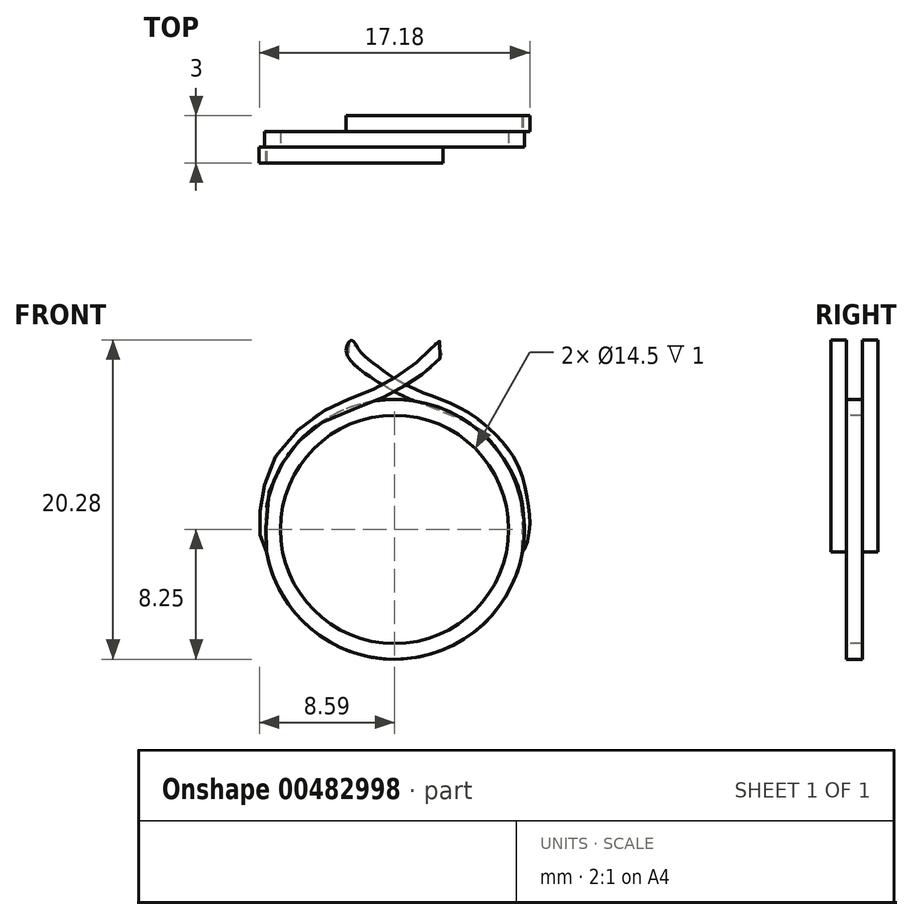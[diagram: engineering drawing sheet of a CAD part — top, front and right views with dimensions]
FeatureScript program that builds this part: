
annotation { "Feature Type Name" : "Feature", "Feature Type Description" : "" }
export const myFeature = defineFeature(function(context is Context, id is Id, definition is map)
    precondition{}
    {
        {
            var Q0;
            Q0=qCreatedBy(makeId("Front.planeOp"),FACE);
            var sketch = newSketch(context, id + "F0", { "sketchPlane" : qUnion([Q0])});
            skCircle(sketch, "E0", {"center": v(0, 0) * mm, "radius": 7.25 * mm});
            skCircle(sketch, "E1", {"center": v(0, 0) * mm, "radius": 8.25 * mm});
            skSolve(sketch);
        }
        {
            var Q0;
            Q0 = qSketchRegion(id + "F0", true);
            extrude(context, id + "F1", {"entities" : qUnion([Q0]), "endBound" : BoundingType.SYMMETRIC, "depth" : 1 * mm});
        }
        {
            var Q0;
            Q0=makeQuery(id+"F1.opExtrude","CAP_FACE",FACE,{"disambiguationData":[OSD([sQuery(id+"F0.wireOp",EDGE,"E0"),sQuery(id+"F0.wireOp",EDGE,"E1")])],"isStart":false});
            var sketch = newSketch(context, id + "F2", { "sketchPlane" : qUnion([Q0])});
            skLineSegment(sketch, "E2", {"start": v(0, 0) * mm, "end": v(-8.12, -1.43) * mm, "construction": true});
            skLineSegment(sketch, "E3", {"start": v(0, 0) * mm, "end": v(8.12, -1.43) * mm, "construction": true});
            skLineSegment(sketch, "E4", {"start": v(0, 0) * mm, "end": v(0, -8.25) * mm, "construction": true});
            skFitSpline(sketch, "E5", {"points": [v(-8.12, -1.43) * mm, v(-8.13, 1.41) * mm, v(-6.93, 4.47) * mm, v(-4.95, 6.6) * mm, v(-1.26, 8.15) * mm, v(0.72, 9.16) * mm, v(1.92, 9.95) * mm, v(3.07, 11.32) * mm, v(2.73, 12.03) * mm, v(2.33, 11.51) * mm, v(1.38, 10.6) * mm, v(-0.48, 9.31) * mm, v(-2.61, 8.38) * mm, v(-4.97, 7.24) * mm, v(-7.7, 4.33) * mm, v(-8.48, 1.6) * mm, v(-8.52, -0.37) * mm, v(-8.12, -1.43) * mm]});
            skSolve(sketch);
        }
        {
            var Q0;
            Q0 = qSketchRegion(id + "F2", true);
            extrude(context, id + "F3", {"entities" : qUnion([Q0]), "operationType" : NewBodyOperationType.ADD, "depth" : 1 * mm});
        }
        {
            var Q0;
            Q0=makeQuery(id+"F1.opExtrude","SWEPT_BODY",BODY,{"disambiguationData":[OSD([sQuery(id+"F0.wireOp",EDGE,"E0"),sQuery(id+"F0.wireOp",EDGE,"E1")])]});
            var Q1;
            Q1=qCreatedBy(makeId("Right.planeOp"),FACE);
            mirror(context, id + "F4", {"entities" : qUnion([Q0]), "mirrorPlane" : qUnion([Q1])});
        }
        {
            var Q0;
            Q0=makeQuery(id+"F4.opPattern","COPY",BODY,{"derivedFrom":makeQuery(id+"F1.opExtrude","SWEPT_BODY",BODY,{"disambiguationData":[OSD([sQuery(id+"F0.wireOp",EDGE,"E0"),sQuery(id+"F0.wireOp",EDGE,"E1")])]}),"instanceName":"1"});
            var Q1;
            Q1=qCreatedBy(makeId("Front.planeOp"),FACE);
            mirror(context, id + "F5", {"entities" : qUnion([Q0]), "mirrorPlane" : qUnion([Q1])});
        }
        {
            var Q0;
            Q0=makeQuery(id+"F4.opPattern","COPY",BODY,{"derivedFrom":makeQuery(id+"F1.opExtrude","SWEPT_BODY",BODY,{"disambiguationData":[OSD([sQuery(id+"F0.wireOp",EDGE,"E0"),sQuery(id+"F0.wireOp",EDGE,"E1")])]}),"instanceName":"1"});
            deleteBodies(context, id + "F6", {"entities" : qUnion([Q0])});
        }
    });
